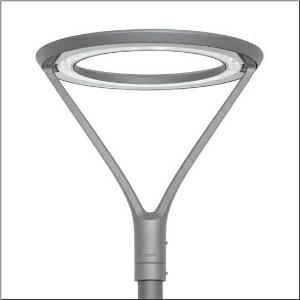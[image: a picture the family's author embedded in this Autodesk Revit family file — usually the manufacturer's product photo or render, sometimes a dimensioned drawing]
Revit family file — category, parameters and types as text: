
# Revit family: dl_r__20_led___st1_2a_5xa51283na008_663b
name_source: partatom
category: Lighting Fixtures
units: mm (PartAtom-declared; Revit-internal decimal feet)

## family parameters
Cut with Voids When Loaded = No
Host = Face
Light Source = No
Part Type = Normal
Room Calculation Point = No
Round Connector Dimension = Use Diameter
Shared = No

## types (1)
- --- (1 x LED 4000K / CRI = 80 (unbekannt), 3010 lm, 4000K)
    Apparent Load = 27 VA
    CIE Flux Codes = 31 69 96 100 100
    Color Rendering = 80
    Color Temperature = 4000K
    Default Elevation = 1800 mm
    Description = DL® 20 LED, mast luminaire, primary light control with reflector, highly specular, primary optical cover: cover, of toughened safety glass of clear glass with excellent transmission level, light distribution: ST1.2a, light emission: direct distribution, primary light characteristic: asymmetric, installation type: post-top, LED High Power LED, rated luminous flux: 3.010 lm, light colour: 840, colour temperature: 4000K, control gear: ECG Plus, control: overheat protection, power reduction, digital communication interface, constant luminous flux control, time-dependent luminous flux control, flexible luminous flux parameterisation, electronic power reduction, mains connection: 220..240V, 50/60Hz, connection cable pre-assembled, cable length: 5 m, start of lifetime: 27 W, end of lifetime: 28 W, reduction: 14 W, luminaire housing, upper part, of cast aluminium, powder-coated, Siteco® metallic grey (DB 702S), diameter: 690 mm, height: 690mm, spigot size: 76mm (post-top), luminaire housing, of cast aluminium, powder-coated, Siteco® metallic grey (DB 702S), protection rating (complete): IP66, insulation class (complete): insulation class II (safety insulation), certification: CE, ENEC, VDE, impact resistance: IK08, permissible ambient temperature for indoor applications: -25..+35°C, standard-compliant lighting for roads and squares, packaging unit: 1 piece

Light Distribution: ST1.2a
    Height = 690 mm
    Lamp = 1 x LED 4000K / CRI >= 80 (unbekannt)
    Lamp Light Flux = 3010 lm
    Lamp count = 1
    Length = 690 mm
    Luminous efficacy = 111 lm/W
    Manufacturer = Siteco
    ModVariant = No
    Model = 5XA51283NA008
    Number of Poles = 1
    OnlyDefault = Yes
    Power Factor = 1
    Product Name = DL® 20 LED | ST1.2a
    Product group = mast luminaire | pylon top
    ProductGroupID = 6100
    Protection Class = Protection class II
    Protection Degree = IP 66
    RLX_Detail_Level = 1
    RlxData = <blob elided: 205901 chars, md5=229ff989>
    Socket = socket
    Standby Power = 0 W
    System Light Flux = 3010 lm
    System Power = 27 W
    Type Comments = factory setting: luminous flux: 100 % | dim-lin: 254 | 358 mA
    Type Image = l_1006001.jpg
    URL = http://relux.com
    VarID = @adj_141421
    Voltage = 0 V
    Weight = 0.00 kg
    Width = 0 mm  [stored 0 ft]

note: [stored X ft] marks values corroborated as IEEE doubles in the binary element streams (Revit-internal decimal feet)

## geometry (parser evidence)
native form markers: Blend x4, Sweep x12
no freeform markers — native parametric forms only
